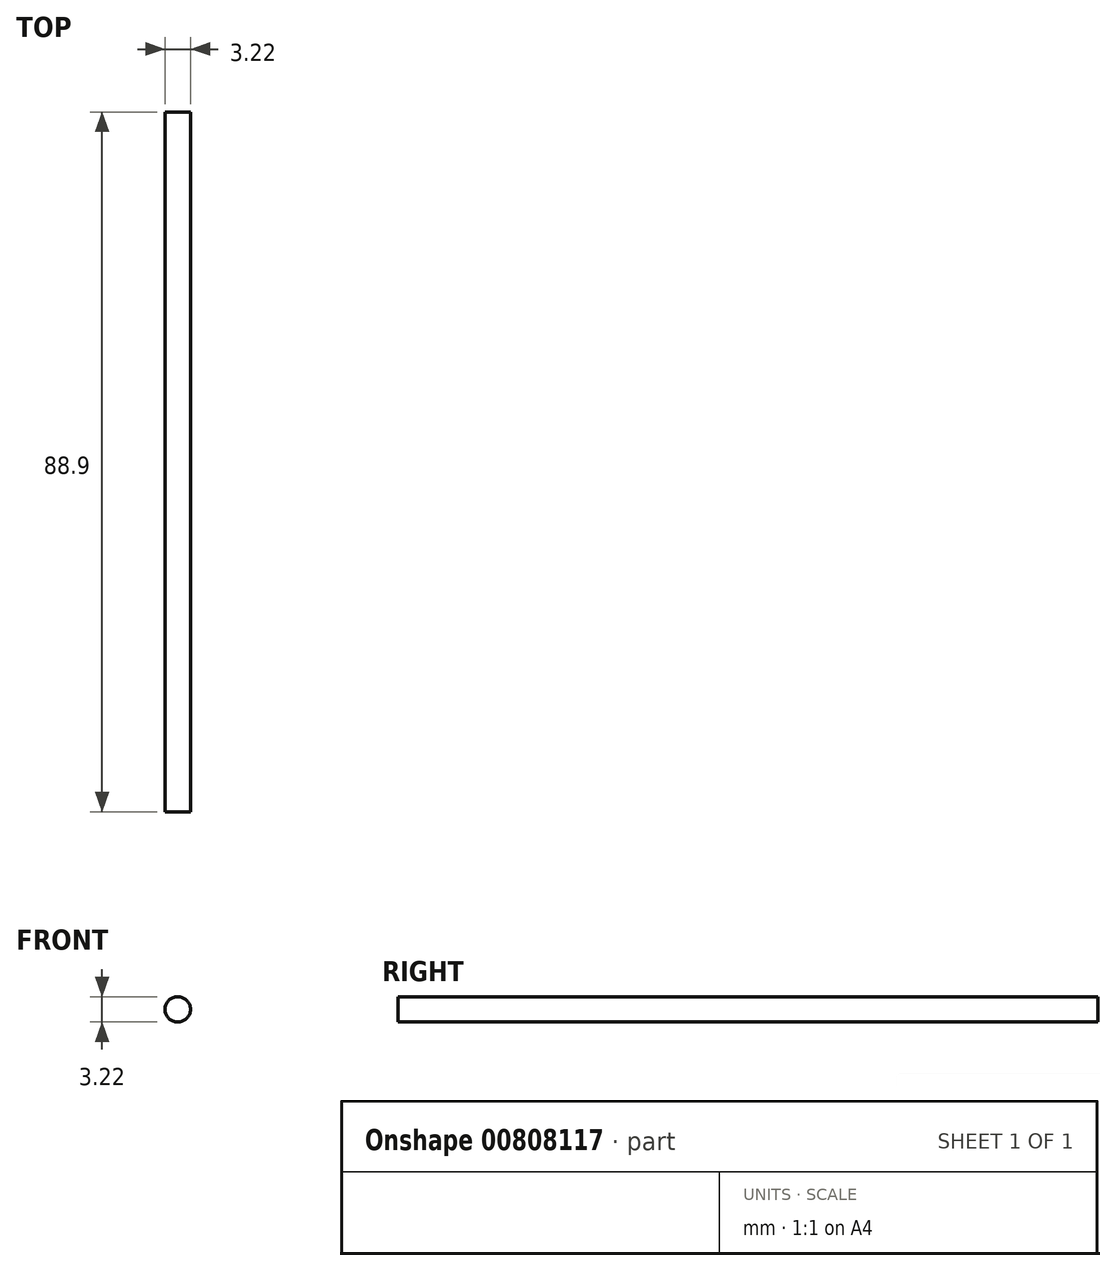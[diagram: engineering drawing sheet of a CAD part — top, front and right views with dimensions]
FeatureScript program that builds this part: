
annotation { "Feature Type Name" : "Feature", "Feature Type Description" : "" }
export const myFeature = defineFeature(function(context is Context, id is Id, definition is map)
    precondition{}
    {
        {
            var Q0;
            Q0=qCreatedBy(makeId("Front.planeOp"),FACE);
            var sketch = newSketch(context, id + "F0", { "sketchPlane" : qUnion([Q0])});
            skCircle(sketch, "E0", {"center": v(-63.51, 54.08) * mm, "radius": 1.61 * mm});
            skSolve(sketch);
        }
        {
            var Q0;
            Q0=qSketchRegion(id+"F0",true);
            extrude(context, id + "F1", {"entities" : qUnion([Q0]), "depth" : 88.9 * mm, "offsetDistance" : 25.4 * mm});
        }
    });
